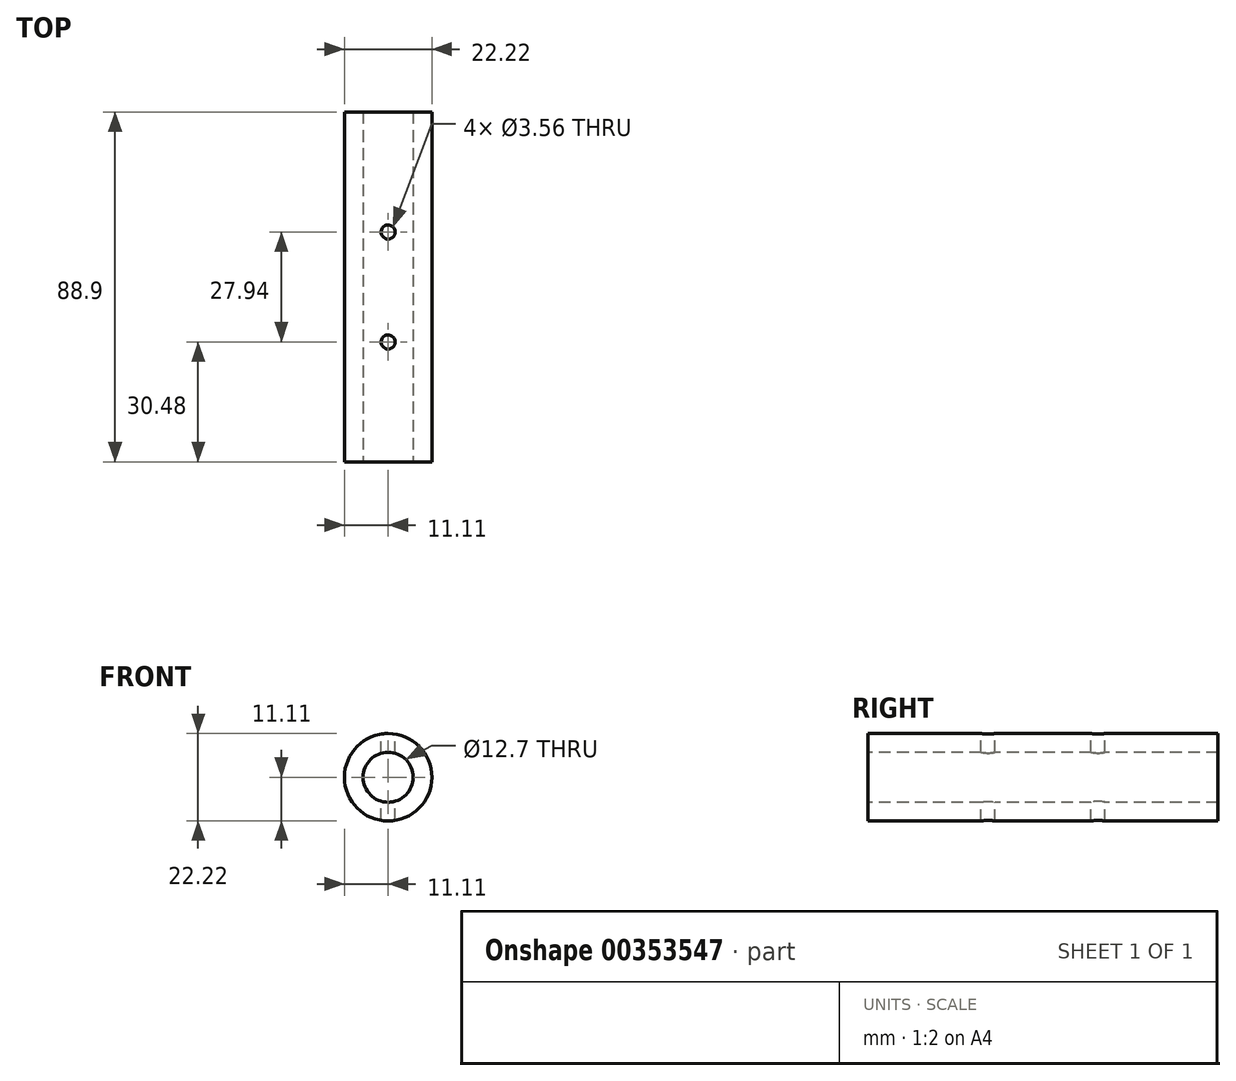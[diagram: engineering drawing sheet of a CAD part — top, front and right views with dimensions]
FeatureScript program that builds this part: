
annotation { "Feature Type Name" : "Feature", "Feature Type Description" : "" }
export const myFeature = defineFeature(function(context is Context, id is Id, definition is map)
    precondition{}
    {
        {
            var Q0;
            Q0=qCreatedBy(makeId("Front.planeOp"),FACE);
            var sketch = newSketch(context, id + "F0", { "sketchPlane" : qUnion([Q0])});
            skCircle(sketch, "E0", {"center": v(0, 0) * mm, "radius": 11.11 * mm});
            skSolve(sketch);
        }
        {
            var Q0;
            Q0 = qSketchRegion(id + "F0", true);
            extrude(context, id + "F1", {"entities" : qUnion([Q0]), "depth" : 88.9 * mm, "symmetric" : true});
        }
        {
            var Q0;
            Q0=makeQuery(id+"F1.opExtrude","CAP_FACE",FACE,{"disambiguationData":[OSD([sQuery(id+"F0.wireOp",EDGE,"E0")])],"isStart":false});
            var sketch = newSketch(context, id + "F2", { "sketchPlane" : qUnion([Q0])});
            skCircle(sketch, "E1", {"center": v(0, 0) * mm, "radius": 6.35 * mm});
            skSolve(sketch);
        }
        {
            var Q0;
            Q0 = qSketchRegion(id + "F2", true);
            extrude(context, id + "F3", {"entities" : qUnion([Q0]), "operationType" : NewBodyOperationType.REMOVE, "endBound" : BoundingType.THROUGH_ALL, "oppositeDirection" : true, "depth" : 25.4 * mm});
        }
        {
            var Q0;
            Q0=qCreatedBy(makeId("Top.planeOp"),FACE);
            var sketch = newSketch(context, id + "F4", { "sketchPlane" : qUnion([Q0])});
            skLineSegment(sketch, "E2.0", {"start": v(11.11, 44.45) * mm, "end": v(-11.11, 44.45) * mm});
            skLineSegment(sketch, "E3", {"start": v(0, 0) * mm, "end": v(0, 13.97) * mm, "construction": true});
            skCircle(sketch, "E4", {"center": v(0, 13.97) * mm, "radius": 1.78 * mm});
            skSolve(sketch);
        }
        {
            var Q0;
            Q0 = qSketchRegion(id + "F4", true);
            extrude(context, id + "F5", {"entities" : qUnion([Q0]), "operationType" : NewBodyOperationType.REMOVE, "oppositeDirection" : true, "depth" : 22.22 * mm, "symmetric" : true});
        }
        {
            var Q0;
            Q0=qCreatedBy(makeId("Top.planeOp"),FACE);
            var sketch = newSketch(context, id + "F6", { "sketchPlane" : qUnion([Q0])});
            skLineSegment(sketch, "E5", {"start": v(0, 0) * mm, "end": v(0, -13.97) * mm, "construction": true});
            skCircle(sketch, "E6", {"center": v(0, -13.97) * mm, "radius": 1.78 * mm});
            skSolve(sketch);
        }
        {
            var Q0;
            Q0 = qSketchRegion(id + "F6", true);
            extrude(context, id + "F7", {"entities" : qUnion([Q0]), "operationType" : NewBodyOperationType.REMOVE, "oppositeDirection" : true, "depth" : 22.22 * mm, "symmetric" : true});
        }
    });
